# Revit family: Electronics_Visual Electronics_ViewSonic_PG800W-HD
name_source: partatom
category: Electrical Equipment
revit_build: Autodesk Revit 2017 (Build: 20171027_0315(x64)
units: mm (PartAtom-declared; Revit-internal decimal feet)

## family parameters
Always vertical = Yes
Cut with Voids When Loaded = No
OmniClass Number = 23.80.00.00
OmniClass Title = Electric Power and Lighting
Panel Configuration = Two Columns, Circuits Across
Part Type = Panelboard
Room Calculation Point = No
Round Connector Dimension = Use Diameter
Shared = No
Work Plane-Based = No

## types (2) — shared parameters
Assembly Code = D50
Audible Noise (Eco) = 33dB
Audible Noise (Normal) = 36dB
Brightness = 5000 ANSI Lumens
Contrast Ratio = 5000:1 (with Eco mode)
Covering Color = Plastic - ViewSonic - White
Diagonal = 3927 mm
Diagonal (Zoom) = 3927 mm
Digital Zoom = 0.8x- 2.0x
Display Colour = 1.07 Billion Colours
Edition number = 1
HDTV Compatibility = 480i, 480p, 576i, 576p, 720p, 1080i, 1080p
Height = 2354 mm
Horizontal Frequency = 15K-102KHz
IAR = 1.33552
Image Aspect Ratio = / : "4  - 3"
Image Size = 30"-300"
Input Lag = 16ms
Keynote = 16800
Keystone = ±40° (Vertical)
Lamp Watt = 370W
Lens = F=2.59-2.87, f=16.88-21.88mm
Light Source Life (Normal) = 2000/2500 (Nor/Eco)
Light Source Type = Lamp
Manufacturer = ViewSonic
Optical Zoom = 1.3X
Product data url = https://www.bimobject.com
Projection Distance = 3801 mm
URL = https://www.viewsonic.com
Vertical Scan Rate = 23-120Hz
Video Compatibility = NTSC, PAL, SECAM
Width = 3144 mm
Zoom Control = 1
a = / : "4  - 3"
b = / : "16 - 9"
c = / : "16 - 10"
zero-valued in all types: Zoom

## per-type parameters (varying)
| type | Description | Lens Shift V. Range | Model | Native Resolution | PG800HD | PG800W | Product Guid | Projection System | Resolution Support | Throw Distance | Throw Ratio |
| PG800W | PG800W - 1280 x 800 Resolution, 5,000 ANSI Lumens, 1.2-1.6 Throw Ratio

Delivering 1280 x 800 resolution and 5000 lumens of brightness, the ViewSonic® PG800W is the ideal WXGA projector for professional installations, large venues, and business and education environments. With its 1.3x optical zoom, centered lens, vertical lens shift, and vertical keystoning, the PG800W provides extreme flexibility even in the most challenging installations. The PG800W boasts a sleek top cover design for quick lamp and accessory access, while an intuitive PortAll® compartment accommodates additional accessories such as an HDBaseT receiver, wireless streaming device, or PC stick. A 4-in-1 power button serves as a central point for LED notifications. Moreover, two HDMI ports and additional audio and video ports allow for extensive connectivity to handle multiple devices without the need to switch cables. Powered by SuperColor™ technology for beautiful image reproduction, and SonicExpert® technology for incredibly clear sound, the PG800W delivers a professional audiovisual performance. | Yes (+7.5%, -0%) | viewsonic_pg800w_projector | 1280x800 | No | Yes | e5bf415c-d9db-4a75-a49a-5304b3389953 | 0.65" WXGA | VGA(640 x 480) to FullHD(1920 x 1080) | 0.78m-10.14m(100" @2.61m) | 1.21-1.57 |
| PG800HD | PG800HD - 1920 x 1080 Resolution, 5,000 ANSI Lumens, 1.15-1.5 Throw Ratio

Delivering 1920 x 1080 resolution and 5000 lumens of brightness, the ViewSonic® PG800HD is the ideal 1080p projector for professional installations, large venues, and business and education environments. With its 1.3x optical zoom, centered lens, vertical lens shift, and vertical keystoning, the PG800HD provides extreme flexibility even in the most challenging installations. The PG800HD boasts a sleek top cover design for quick lamp and accessory access, while an intuitive PortAll® compartment accommodates additional accessories such as an HDBaseT receiver, wireless streaming device, or PC stick. A 4-in-1 power button serves as a central point for LED notifications. Moreover, two HDMI ports and additional audio and video ports allow for extensive connectivity to handle multiple devices without the need to switch cables. Powered by SuperColor™ technology for beautiful image reproduction, and SonicExpert® technology for incredibly clear sound, the PG800HD delivers a professional audiovisual performance. | Yes (+7%, -0%) | viewsonic_pg800hd_projector | 1920x1080 | Yes | No | 281c833e-fb8e-4a2a-8bd1-956cee5ce0f0 | 0.65" 1080p | VGA(640 x 480) to WUXGA_RB(1920 x 1200) | 0.76m-9.96m(100" @2.55m) | 1.15-1.5 |

## geometry (parser evidence)
native form markers: Sweep x17
no freeform markers — native parametric forms only
